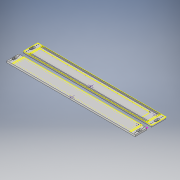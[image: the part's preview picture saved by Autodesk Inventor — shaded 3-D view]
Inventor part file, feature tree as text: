
AUTODESK INVENTOR PART (.ipt)
format: ipt  version: 2018.3 (Build 223284000, 284)  size: 279,040 bytes
history: native  units: in
note: dims shown in document units (in); Inventor stores cm internally (conversion verified against a paired STEP export)
features: extrude x5, other x4, hole x3, projected_geometry x3
ambient origin geometry x8: Origin, YZ Plane, XZ Plane, XY Plane, X Axis, Y Axis, Z Axis, Center Point
bodies: Solid1 (feature_tree)
feature tree (15):
  other  "Base Sketch"
  extrude  "Base"  Depth=50.0in
  extrude  "Lower Level"  Depth=6.0in
  other  "Track Sketch"
  extrude  "Tracks Cut"  Depth=2.0in
  extrude  "Pocket Side"  Depth=2.0in
  other  "Origin Sketch"
  other  "Handles Sketch"
  extrude  "Extrusion6"  Depth=0.75in TaperAngle=0.0deg
  hole  "Hole1"  [1 undecoded]
  hole  "Hole3"  [1 undecoded]
  hole  "Hole2"  [1 undecoded]
  projected_geometry  "Projected Loop3"
  projected_geometry  "Projected Loop4"
  projected_geometry  "Projected Loop5"
note: 3 required parameter values undecoded (feature->parameter linkage not recoverable at this tier; creation-order binding heuristic only, values carry confidence <= 0.55)
